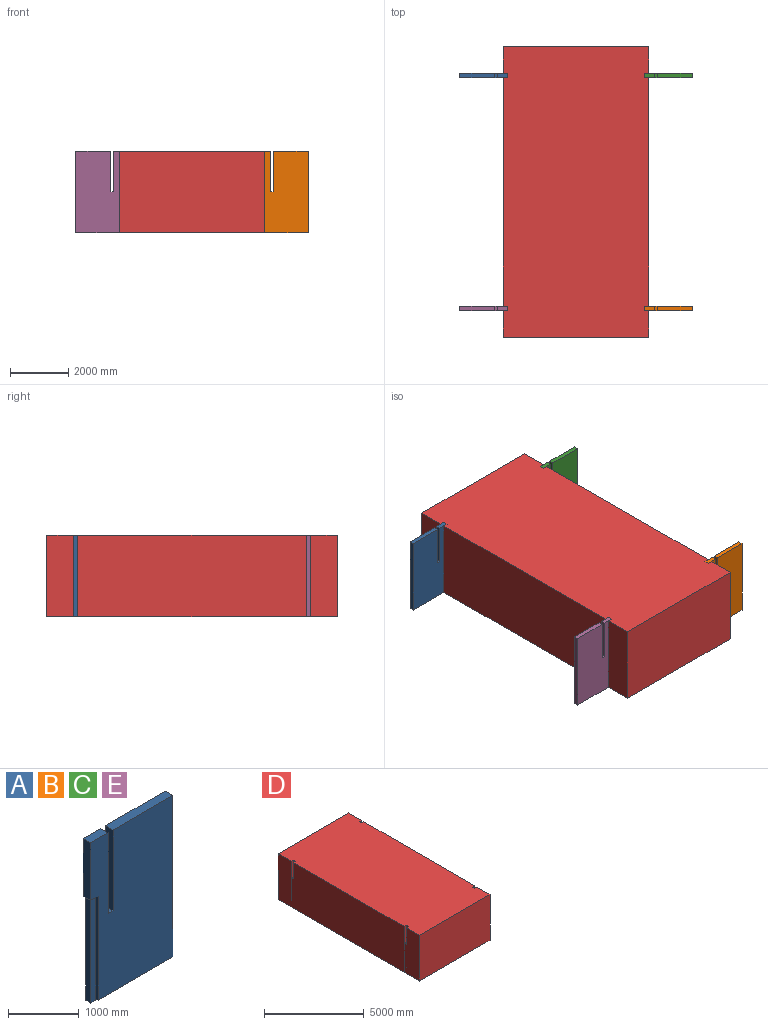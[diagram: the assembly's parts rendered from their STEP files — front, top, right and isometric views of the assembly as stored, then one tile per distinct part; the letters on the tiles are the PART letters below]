
ASSEMBLY  parts=5 mates=4
PART A: 17 faces, bbox 1650x150x2800 mm
  f0: plane 1200x150mm, normal (0,0,1), area 180000mm2, adj f1,f8,f11,f15
  f1: plane 2800x1650mm, normal (0,-1,0), area 4210000mm2, adj f0,f5,f6,f7,f8,f9,f10,f14
  f2: plane 1800x100mm, normal (-1,0,0), area 180000mm2, adj f3,f5,f12,f13
  f3: plane 100x100mm, normal (0,0,-1), area 10000mm2, adj f2,f4,f12,f13
  f4: plane 1800x100mm, normal (1,0,0), area 180000mm2, adj f3,f5,f12,f13
  f5: plane 150x150mm, normal (0,0,-1), area 12500mm2, adj f1,f2,f4,f6,f10,f11,f12,f13
  f6: plane 1800x150mm, normal (-1,0,0), area 270000mm2, adj f1,f5,f7,f11
  f7: plane 1500x150mm, normal (0,0,-1), area 225000mm2, adj f1,f6,f8,f11
  f8: plane 2800x150mm, normal (1,0,0), area 420000mm2, adj f0,f1,f7,f11
  f9: plane 350x150mm, normal (0,0,1), area 52500mm2, adj f1,f10,f11,f14
  f10: plane 1000x150mm, normal (-1,0,0), area 150000mm2, adj f1,f5,f9,f11
  f11: plane 2800x1650mm, normal (0,1,0), area 4210000mm2, adj f0,f5,f6,f7,f8,f9,f10,f14
  f12: plane 1800x100mm, normal (0,1,0), area 180000mm2, adj f2,f3,f4,f5
  f13: plane 1800x100mm, normal (0,-1,0), area 180000mm2, adj f2,f3,f4,f5
  f14: plane 1400x150mm, normal (1,0,0), area 210000mm2, adj f1,f9,f11,f16
  f15: plane 1400x150mm, normal (-1,0,0), area 210000mm2, adj f0,f1,f11,f16
  f16: plane 150x100mm, normal (0,0,1), area 15000mm2, adj f1,f11,f14,f15
PART B: same geometry as A
PART C: same geometry as A
PART D: 38 faces, bbox 5000x10000x2800 mm
  f0: plane 10000x5000mm, normal (0,0,-1), area 49960000mm2, adj f5,f6,f7,f8,f22,f23,f24,f25
  f1: plane 150x150mm, normal (0,0,1), area 12500mm2, adj f6,f10,f11,f12,f34,f35,f36,f37
  f2: plane 150x150mm, normal (0,0,1), area 12500mm2, adj f5,f13,f14,f15,f30,f31,f32,f33
  f3: plane 150x150mm, normal (0,0,1), area 12500mm2, adj f5,f16,f17,f18,f26,f27,f28,f29
  f4: plane 150x150mm, normal (0,0,1), area 12500mm2, adj f6,f19,f20,f21,f22,f23,f24,f25
  f5: plane 10000x2800mm, normal (1,0,0), area 27700000mm2, adj f0,f2,f3,f7,f8,f9,f13,f15
  f6: plane 10000x2800mm, normal (-1,0,0), area 27700000mm2, adj f0,f1,f4,f7,f8,f9,f10,f12
  f7: plane 5000x2800mm, normal (0,-1,0), area 14000000mm2, adj f0,f5,f6,f9
  f8: plane 5000x2800mm, normal (0,1,0), area 14000000mm2, adj f0,f5,f6,f9
  f9: plane 10000x5000mm, normal (0,0,1), area 49910000mm2, adj f5,f6,f7,f8,f10,f11,f12,f13
  f10: plane 1000x150mm, normal (0,1,0), area 150000mm2, adj f1,f6,f9,f11
  f11: plane 1000x150mm, normal (-1,0,0), area 150000mm2, adj f1,f9,f10,f12
  f12: plane 1000x150mm, normal (0,-1,0), area 150000mm2, adj f1,f6,f9,f11
  f13: plane 1000x150mm, normal (0,-1,0), area 150000mm2, adj f2,f5,f9,f14
  f14: plane 1000x150mm, normal (1,0,0), area 150000mm2, adj f2,f9,f13,f15
  f15: plane 1000x150mm, normal (0,1,0), area 150000mm2, adj f2,f5,f9,f14
  f16: plane 1000x150mm, normal (0,-1,0), area 150000mm2, adj f3,f5,f9,f17
  f17: plane 1000x150mm, normal (1,0,0), area 150000mm2, adj f3,f9,f16,f18
  f18: plane 1000x150mm, normal (0,1,0), area 150000mm2, adj f3,f5,f9,f17
  f19: plane 1000x150mm, normal (0,1,0), area 150000mm2, adj f4,f6,f9,f20
  f20: plane 1000x150mm, normal (-1,0,0), area 150000mm2, adj f4,f9,f19,f21
  f21: plane 1000x150mm, normal (0,-1,0), area 150000mm2, adj f4,f6,f9,f20
  f22: plane 1800x100mm, normal (0,-1,0), area 180000mm2, adj f0,f4,f23,f25
  f23: plane 1800x100mm, normal (1,0,0), area 180000mm2, adj f0,f4,f22,f24
  f24: plane 1800x100mm, normal (0,1,0), area 180000mm2, adj f0,f4,f23,f25
  f25: plane 1800x100mm, normal (-1,0,0), area 180000mm2, adj f0,f4,f22,f24
  f26: plane 1800x100mm, normal (0,-1,0), area 180000mm2, adj f0,f3,f27,f29
  f27: plane 1800x100mm, normal (1,0,0), area 180000mm2, adj f0,f3,f26,f28
  f28: plane 1800x100mm, normal (0,1,0), area 180000mm2, adj f0,f3,f27,f29
  f29: plane 1800x100mm, normal (-1,0,0), area 180000mm2, adj f0,f3,f26,f28
  f30: plane 1800x100mm, normal (0,-1,0), area 180000mm2, adj f0,f2,f31,f33
  f31: plane 1800x100mm, normal (1,0,0), area 180000mm2, adj f0,f2,f30,f32
  f32: plane 1800x100mm, normal (0,1,0), area 180000mm2, adj f0,f2,f31,f33
  f33: plane 1800x100mm, normal (-1,0,0), area 180000mm2, adj f0,f2,f30,f32
  f34: plane 1800x100mm, normal (0,-1,0), area 180000mm2, adj f0,f1,f35,f37
  f35: plane 1800x100mm, normal (1,0,0), area 180000mm2, adj f0,f1,f34,f36
  f36: plane 1800x100mm, normal (0,1,0), area 180000mm2, adj f0,f1,f35,f37
  f37: plane 1800x100mm, normal (-1,0,0), area 180000mm2, adj f0,f1,f34,f36
PART E: same geometry as A
PLACE A rot(axis=(0,0,-1),180deg) t=(-3645.1,4179.66,586.55)mm
PLACE B t=(3132.97,-3670.34,586.55)mm
PLACE C t=(3132.97,4329.66,586.55)mm
PLACE D t=(-309.48,159.02,-796.25)mm fixed
PLACE E rot(axis=(0,0,-1),180deg) t=(-3645.1,-3820.34,586.55)mm
MATE parallel C.f10 <-> D.f14  axis (-1,0,0) through (2093.93,4254.66,1503.75)mm
MATE parallel D.f17 <-> B.f10  axis (1,0,0) through (2093.93,-3745.34,1503.75)mm
MATE parallel E.f10 <-> D.f20  axis (1,0,0) through (-2606.07,-3745.34,1503.75)mm
MATE parallel A.f10 <-> D.f11  axis (1,0,0) through (-2606.07,4254.66,1503.75)mm
